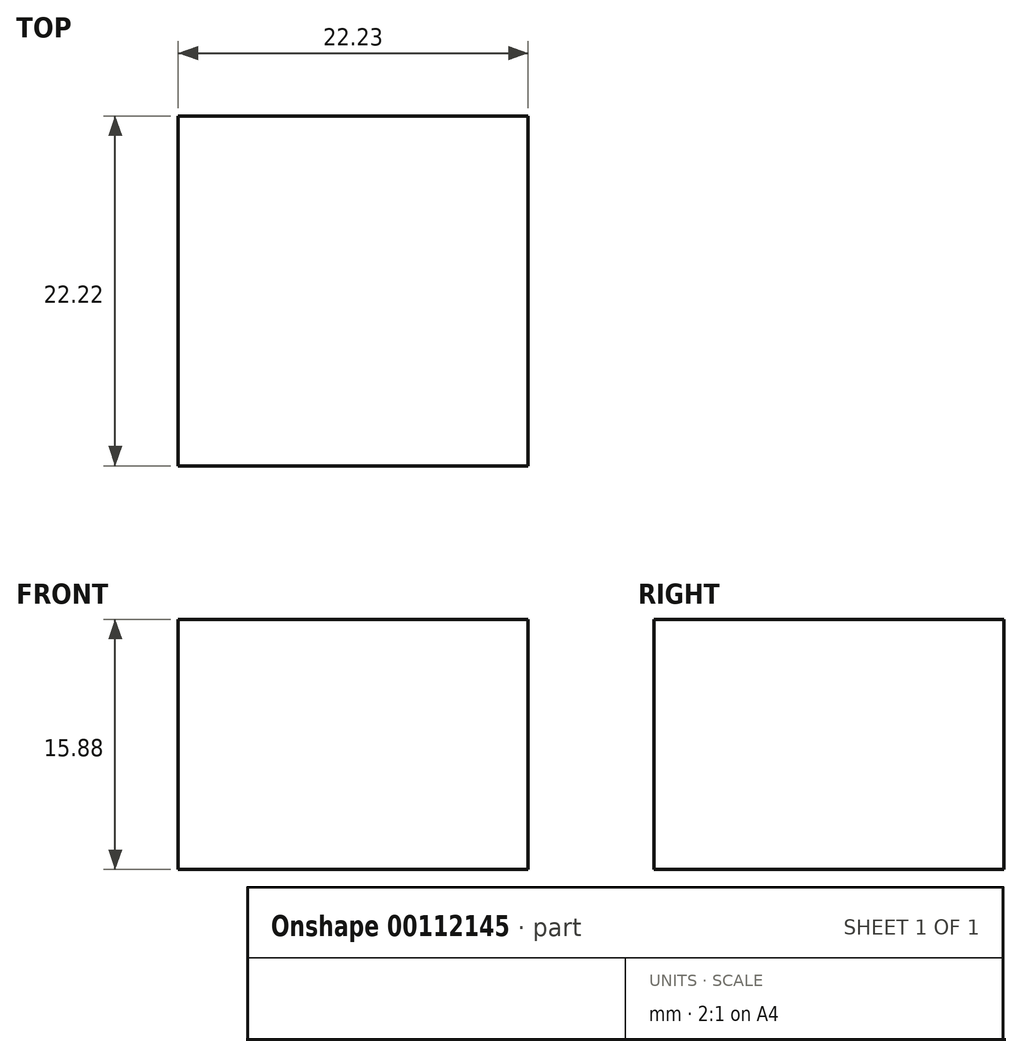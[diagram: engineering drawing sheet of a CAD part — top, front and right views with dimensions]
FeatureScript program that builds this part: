
annotation { "Feature Type Name" : "Feature", "Feature Type Description" : "" }
export const myFeature = defineFeature(function(context is Context, id is Id, definition is map)
    precondition{}
    {
        {
            var Q0;
            Q0=qCreatedBy(makeId("Top.planeOp"),FACE);
            var sketch = newSketch(context, id + "F0", { "sketchPlane" : qUnion([Q0])});
            skLineSegment(sketch, "E0.bottom", {"start": v(-20.25, -17.8) * mm, "end": v(1.98, -17.8) * mm});
            skLineSegment(sketch, "E0.top", {"start": v(-20.25, 4.43) * mm, "end": v(1.98, 4.43) * mm});
            skLineSegment(sketch, "E0.left", {"start": v(-20.25, -17.8) * mm, "end": v(-20.25, 4.43) * mm});
            skLineSegment(sketch, "E0.right", {"start": v(1.98, -17.8) * mm, "end": v(1.98, 4.43) * mm});
            skSolve(sketch);
        }
        {
            var Q0;
            Q0=makeQuery(id+"F0.imprint","IMPRINT",FACE,{"disambiguationData":[TD([[makeQuery(id+"F0.imprint","IMPRINT",EDGE,{"derivedFrom":sQuery(id+"F0.wireOp",EDGE,"E0.bottom")}),1.0]])]});
            extrude(context, id + "F1", {"entities" : qUnion([Q0]), "depth" : 15.88 * mm});
        }
    });
